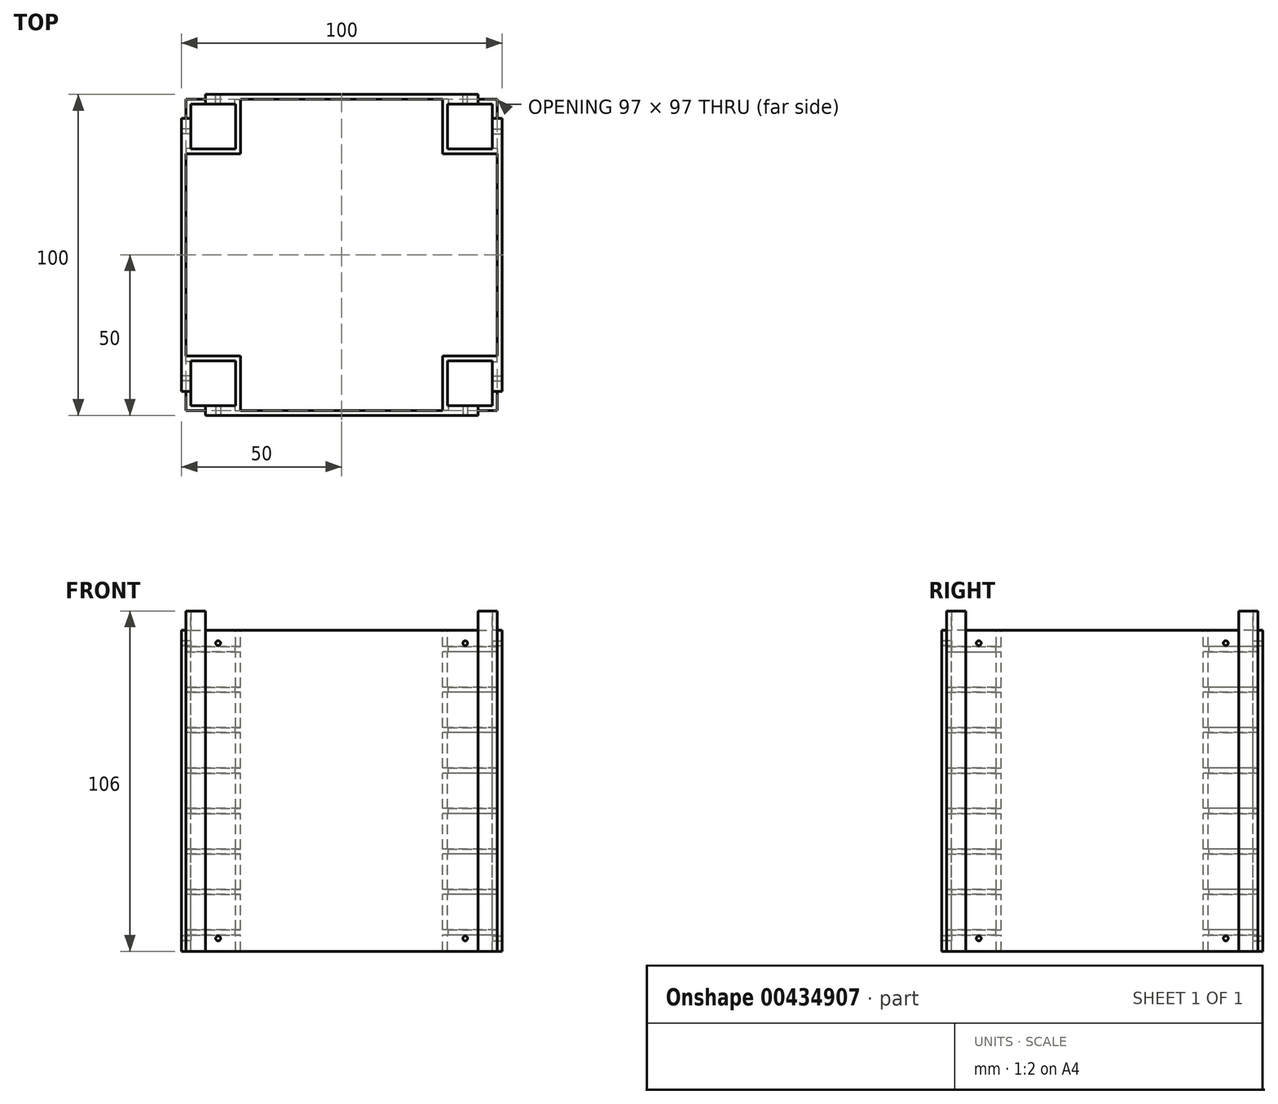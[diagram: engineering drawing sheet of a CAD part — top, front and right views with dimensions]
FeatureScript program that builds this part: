
annotation { "Feature Type Name" : "Feature", "Feature Type Description" : "" }
export const myFeature = defineFeature(function(context is Context, id is Id, definition is map)
    precondition{}
    {
        {
            var Q0;
            Q0=qCreatedBy(makeId("Top.planeOp"),FACE);
            var sketch = newSketch(context, id + "F0", { "sketchPlane" : qUnion([Q0])});
            skLineSegment(sketch, "E0", {"start": v(0, 97) * mm, "end": v(0, 80) * mm});
            skLineSegment(sketch, "E1", {"start": v(0, 80) * mm, "end": v(17, 80) * mm});
            skLineSegment(sketch, "E2", {"start": v(17, 80) * mm, "end": v(17, 97) * mm});
            skLineSegment(sketch, "E3", {"start": v(17, 97) * mm, "end": v(0, 97) * mm});
            skLineSegment(sketch, "E4", {"start": v(0, 97) * mm, "end": v(0, 95.5) * mm});
            skLineSegment(sketch, "E5", {"start": v(17, 97) * mm, "end": v(17, 95.5) * mm});
            skLineSegment(sketch, "E6", {"start": v(0, 80) * mm, "end": v(1.5, 80) * mm});
            skLineSegment(sketch, "E7", {"start": v(17, 80) * mm, "end": v(15.5, 80) * mm});
            skLineSegment(sketch, "E8", {"start": v(1.5, 95.5) * mm, "end": v(15.5, 95.5) * mm});
            skLineSegment(sketch, "E9", {"start": v(15.5, 81.5) * mm, "end": v(1.5, 81.5) * mm});
            skLineSegment(sketch, "E10", {"start": v(1.5, 95.5) * mm, "end": v(1.5, 81.5) * mm});
            skLineSegment(sketch, "E11", {"start": v(15.5, 95.5) * mm, "end": v(15.5, 81.5) * mm});
            skLineSegment(sketch, "E12.1.0.0", {"start": v(80, 97) * mm, "end": v(80, 95.5) * mm});
            skLineSegment(sketch, "E12.1.0.1", {"start": v(81.5, 95.5) * mm, "end": v(81.5, 81.5) * mm});
            skLineSegment(sketch, "E12.1.0.2", {"start": v(97, 80) * mm, "end": v(95.5, 80) * mm});
            skLineSegment(sketch, "E12.1.0.3", {"start": v(97, 97) * mm, "end": v(80, 97) * mm});
            skLineSegment(sketch, "E12.1.0.4", {"start": v(80, 97) * mm, "end": v(80, 80) * mm});
            skLineSegment(sketch, "E12.1.0.5", {"start": v(81.5, 95.5) * mm, "end": v(95.5, 95.5) * mm});
            skLineSegment(sketch, "E12.1.0.6", {"start": v(80, 80) * mm, "end": v(97, 80) * mm});
            skLineSegment(sketch, "E12.1.0.7", {"start": v(97, 80) * mm, "end": v(97, 97) * mm});
            skLineSegment(sketch, "E12.1.0.8", {"start": v(95.5, 81.5) * mm, "end": v(81.5, 81.5) * mm});
            skLineSegment(sketch, "E12.1.0.9", {"start": v(95.5, 95.5) * mm, "end": v(95.5, 81.5) * mm});
            skLineSegment(sketch, "E12.1.0.10", {"start": v(97, 97) * mm, "end": v(97, 95.5) * mm});
            skLineSegment(sketch, "E12.1.0.11", {"start": v(80, 80) * mm, "end": v(81.5, 80) * mm});
            skLineSegment(sketch, "E13.0.1.0", {"start": v(95.5, 15.5) * mm, "end": v(95.5, 1.5) * mm});
            skLineSegment(sketch, "E13.0.1.1", {"start": v(97, 0) * mm, "end": v(95.5, 0) * mm});
            skLineSegment(sketch, "E13.0.1.2", {"start": v(80, 0) * mm, "end": v(97, 0) * mm});
            skLineSegment(sketch, "E13.0.1.3", {"start": v(80, 17) * mm, "end": v(80, 15.5) * mm});
            skLineSegment(sketch, "E13.0.1.4", {"start": v(80, 17) * mm, "end": v(80, 0) * mm});
            skLineSegment(sketch, "E13.0.1.5", {"start": v(97, 0) * mm, "end": v(97, 17) * mm});
            skLineSegment(sketch, "E13.0.1.6", {"start": v(81.5, 15.5) * mm, "end": v(81.5, 1.5) * mm});
            skLineSegment(sketch, "E13.0.1.7", {"start": v(81.5, 15.5) * mm, "end": v(95.5, 15.5) * mm});
            skLineSegment(sketch, "E13.0.1.8", {"start": v(95.5, 1.5) * mm, "end": v(81.5, 1.5) * mm});
            skLineSegment(sketch, "E13.0.1.9", {"start": v(97, 17) * mm, "end": v(80, 17) * mm});
            skLineSegment(sketch, "E13.0.1.10", {"start": v(97, 17) * mm, "end": v(97, 15.5) * mm});
            skLineSegment(sketch, "E13.0.1.11", {"start": v(80, 0) * mm, "end": v(81.5, 0) * mm});
            skLineSegment(sketch, "E14.2.0.0", {"start": v(15.5, 1.5) * mm, "end": v(1.5, 1.5) * mm});
            skLineSegment(sketch, "E14.2.0.3", {"start": v(1.5, 15.5) * mm, "end": v(1.5, 1.5) * mm});
            skLineSegment(sketch, "E14.2.0.4", {"start": v(17, 17) * mm, "end": v(0, 17) * mm});
            skLineSegment(sketch, "E14.2.0.5", {"start": v(0, 0) * mm, "end": v(17, 0) * mm});
            skLineSegment(sketch, "E14.2.0.6", {"start": v(0, 17) * mm, "end": v(0, 0) * mm});
            skLineSegment(sketch, "E14.2.0.7", {"start": v(1.5, 15.5) * mm, "end": v(15.5, 15.5) * mm});
            skLineSegment(sketch, "E14.2.0.8", {"start": v(15.5, 15.5) * mm, "end": v(15.5, 1.5) * mm});
            skLineSegment(sketch, "E14.2.0.9", {"start": v(17, 0) * mm, "end": v(17, 17) * mm});
            skLineSegment(sketch, "E14.2.0.10", {"start": v(17, 0) * mm, "end": v(15.5, 0) * mm});
            skLineSegment(sketch, "E14.2.0.11", {"start": v(17, 17) * mm, "end": v(17, 15.5) * mm});
            skLineSegment(sketch, "E14.2.0.12", {"start": v(0, 17) * mm, "end": v(0, 15.5) * mm});
            skLineSegment(sketch, "E14.2.0.13", {"start": v(0, 0) * mm, "end": v(1.5, 0) * mm});
            skSolve(sketch);
        }
        {
            var Q0;
            Q0 = qSketchRegion(id + "F0", true);
            extrude(context, id + "F1", {"entities" : qUnion([Q0]), "oppositeDirection" : true, "depth" : 100 * mm});
        }
        {
            var Q0;
            Q0=makeQuery(id+"F1.opExtrude","CAP_FACE",FACE,{"disambiguationData":[OSD([sQuery(id+"F0.wireOp",EDGE,"E0"),sQuery(id+"F0.wireOp",EDGE,"E1"),sQuery(id+"F0.wireOp",EDGE,"E2"),sQuery(id+"F0.wireOp",EDGE,"E3"),sQuery(id+"F0.wireOp",EDGE,"E4"),sQuery(id+"F0.wireOp",EDGE,"E5"),sQuery(id+"F0.wireOp",EDGE,"E6"),sQuery(id+"F0.wireOp",EDGE,"E7"),sQuery(id+"F0.wireOp",EDGE,"E8"),sQuery(id+"F0.wireOp",EDGE,"E9"),sQuery(id+"F0.wireOp",EDGE,"E10"),sQuery(id+"F0.wireOp",EDGE,"E11")])],"isStart":true});
            var sketch = newSketch(context, id + "F2", { "sketchPlane" : qUnion([Q0])});
            skLineSegment(sketch, "E15", {"start": v(0, 97) * mm, "end": v(0, 91) * mm});
            skLineSegment(sketch, "E16", {"start": v(0, 91) * mm, "end": v(-1.5, 91) * mm});
            skLineSegment(sketch, "E17", {"start": v(0, 0) * mm, "end": v(0, 6) * mm});
            skLineSegment(sketch, "E18", {"start": v(0, 6) * mm, "end": v(-1.5, 6) * mm});
            skLineSegment(sketch, "E19", {"start": v(-1.5, 6) * mm, "end": v(-1.5, 91) * mm});
            skLineSegment(sketch, "E20", {"start": v(0, 91) * mm, "end": v(0, 6) * mm});
            skLineSegment(sketch, "E21", {"start": v(0, 0) * mm, "end": v(6, 0) * mm});
            skLineSegment(sketch, "E22", {"start": v(6, 0) * mm, "end": v(6, -1.5) * mm});
            skLineSegment(sketch, "E23", {"start": v(6, -1.5) * mm, "end": v(91, -1.5) * mm});
            skLineSegment(sketch, "E24", {"start": v(91, -1.5) * mm, "end": v(91, 0) * mm});
            skLineSegment(sketch, "E25", {"start": v(91, 0) * mm, "end": v(6, 0) * mm});
            skLineSegment(sketch, "E26.0", {"start": v(97, 97) * mm, "end": v(80, 97) * mm});
            skLineSegment(sketch, "E27.0", {"start": v(97, 80) * mm, "end": v(97, 97) * mm});
            skLineSegment(sketch, "E28.0", {"start": v(97, 17) * mm, "end": v(97, 0) * mm});
            skLineSegment(sketch, "E29.0", {"start": v(97, 17) * mm, "end": v(80, 17) * mm});
            skLineSegment(sketch, "E30", {"start": v(97, 97) * mm, "end": v(97, 91) * mm});
            skLineSegment(sketch, "E31", {"start": v(97, 91) * mm, "end": v(98.5, 91) * mm});
            skLineSegment(sketch, "E32", {"start": v(98.5, 91) * mm, "end": v(98.5, 6) * mm});
            skLineSegment(sketch, "E33", {"start": v(98.5, 6) * mm, "end": v(97, 6) * mm});
            skLineSegment(sketch, "E34", {"start": v(97, 6) * mm, "end": v(97, 80) * mm});
            skLineSegment(sketch, "E35", {"start": v(0, 97) * mm, "end": v(6, 97) * mm});
            skLineSegment(sketch, "E36", {"start": v(6, 97) * mm, "end": v(91, 97) * mm});
            skLineSegment(sketch, "E37", {"start": v(91, 97) * mm, "end": v(91, 98.5) * mm});
            skLineSegment(sketch, "E38", {"start": v(91, 98.5) * mm, "end": v(6, 98.5) * mm});
            skLineSegment(sketch, "E39", {"start": v(6, 98.5) * mm, "end": v(6, 97) * mm});
            skSolve(sketch);
        }
        {
            var Q0;
            Q0 = qSketchRegion(id + "F2", true);
            extrude(context, id + "F3", {"entities" : qUnion([Q0]), "oppositeDirection" : true, "depth" : 100 * mm, "offsetDistance" : 25 * mm});
        }
        {
            var Q0;
            Q0=makeQuery(id+"F1.opExtrude","CAP_FACE",FACE,{"disambiguationData":[OSD([sQuery(id+"F0.wireOp",EDGE,"E0"),sQuery(id+"F0.wireOp",EDGE,"E1"),sQuery(id+"F0.wireOp",EDGE,"E2"),sQuery(id+"F0.wireOp",EDGE,"E3"),sQuery(id+"F0.wireOp",EDGE,"E4"),sQuery(id+"F0.wireOp",EDGE,"E5"),sQuery(id+"F0.wireOp",EDGE,"E6"),sQuery(id+"F0.wireOp",EDGE,"E7"),sQuery(id+"F0.wireOp",EDGE,"E8"),sQuery(id+"F0.wireOp",EDGE,"E9"),sQuery(id+"F0.wireOp",EDGE,"E10"),sQuery(id+"F0.wireOp",EDGE,"E11")])],"isStart":true});
            var sketch = newSketch(context, id + "F4", { "sketchPlane" : qUnion([Q0])});
            skLineSegment(sketch, "E40.0", {"start": v(0, 97) * mm, "end": v(0, 91) * mm});
            skLineSegment(sketch, "E41.0", {"start": v(17, 97) * mm, "end": v(0, 97) * mm});
            skPoint(sketch, "E42.0", {"position": v(-0.75, 91) * mm});
            skLineSegment(sketch, "E43.0", {"start": v(0, 91) * mm, "end": v(-1.5, 91) * mm});
            skLineSegment(sketch, "E44.0", {"start": v(6, 98.5) * mm, "end": v(6, 97) * mm});
            skLineSegment(sketch, "E45.0.0", {"start": v(91, 98.5) * mm, "end": v(6, 98.5) * mm});
            skLineSegment(sketch, "E45.0.2", {"start": v(17, 97) * mm, "end": v(91, 97) * mm});
            skLineSegment(sketch, "E46.0", {"start": v(97, 97) * mm, "end": v(91, 97) * mm});
            skLineSegment(sketch, "E47.0", {"start": v(97, 91) * mm, "end": v(97, 97) * mm});
            skLineSegment(sketch, "E48.0", {"start": v(97, 6) * mm, "end": v(97, 0) * mm});
            skLineSegment(sketch, "E49.0", {"start": v(91, 0) * mm, "end": v(97, 0) * mm});
            skLineSegment(sketch, "E50.0", {"start": v(0, 6) * mm, "end": v(0, 0) * mm});
            skLineSegment(sketch, "E51.0", {"start": v(0, 0) * mm, "end": v(6, 0) * mm});
            skLineSegment(sketch, "E52.0", {"start": v(1.5, 6) * mm, "end": v(1.5, 1.5) * mm});
            skLineSegment(sketch, "E53.0", {"start": v(15.5, 1.5) * mm, "end": v(1.5, 1.5) * mm});
            skLineSegment(sketch, "E54.0", {"start": v(95.5, 6) * mm, "end": v(95.5, 1.5) * mm});
            skLineSegment(sketch, "E55.0", {"start": v(95.5, 95.5) * mm, "end": v(95.5, 91) * mm});
            skLineSegment(sketch, "E56.0", {"start": v(91, 95.5) * mm, "end": v(95.5, 95.5) * mm});
            skLineSegment(sketch, "E57.0", {"start": v(1.5, 95.5) * mm, "end": v(6, 95.5) * mm});
            skLineSegment(sketch, "E58.0", {"start": v(1.5, 95.5) * mm, "end": v(1.5, 81.5) * mm});
            skLineSegment(sketch, "E59", {"start": v(0, 91) * mm, "end": v(1.5, 91) * mm});
            skLineSegment(sketch, "E60", {"start": v(1.5, 91) * mm, "end": v(1.5, 95.5) * mm});
            skLineSegment(sketch, "E61", {"start": v(6, 95.5) * mm, "end": v(6, 97) * mm});
            skLineSegment(sketch, "E62", {"start": v(0, 97) * mm, "end": v(6, 97) * mm});
            skLineSegment(sketch, "E63", {"start": v(91, 97) * mm, "end": v(91, 95.5) * mm});
            skLineSegment(sketch, "E64", {"start": v(95.5, 91) * mm, "end": v(95.5, 95.5) * mm});
            skLineSegment(sketch, "E65", {"start": v(95.5, 91) * mm, "end": v(97, 91) * mm});
            skLineSegment(sketch, "E66", {"start": v(6, 0) * mm, "end": v(6, 1.5) * mm});
            skLineSegment(sketch, "E67", {"start": v(6, 1.5) * mm, "end": v(6, 0) * mm});
            skLineSegment(sketch, "E68", {"start": v(0, 6) * mm, "end": v(1.5, 6) * mm});
            skLineSegment(sketch, "E69", {"start": v(97, 6) * mm, "end": v(95.5, 6) * mm});
            skLineSegment(sketch, "E70", {"start": v(91, 0) * mm, "end": v(91, 1.5) * mm});
            skLineSegment(sketch, "E71", {"start": v(91, 1.5) * mm, "end": v(95.5, 1.5) * mm});
            skPoint(sketch, "E72.orphan", {"position": v(0, 80) * mm});
            skPoint(sketch, "E73.orphan", {"position": v(15.5, 95.5) * mm});
            skPoint(sketch, "E74.orphan", {"position": v(80, 97) * mm});
            skPoint(sketch, "E75.0.end.orphan", {"position": v(98.5, 91) * mm});
            skPoint(sketch, "E76.orphan", {"position": v(95.5, 81.5) * mm});
            skPoint(sketch, "E77.orphan", {"position": v(81.5, 95.5) * mm});
            skPoint(sketch, "E78.orphan", {"position": v(97, 80) * mm});
            skPoint(sketch, "E79.orphan", {"position": v(1.5, 15.5) * mm});
            skPoint(sketch, "E80.start.orphan", {"position": v(-1.5, 6) * mm});
            skPoint(sketch, "E81.orphan", {"position": v(0, 17) * mm});
            skPoint(sketch, "E82.0.end.orphan", {"position": v(6, -1.5) * mm});
            skPoint(sketch, "E83.orphan", {"position": v(17, 0) * mm});
            skPoint(sketch, "E84.orphan", {"position": v(80, 0) * mm});
            skPoint(sketch, "E85.0.start.orphan", {"position": v(91, -1.5) * mm});
            skPoint(sketch, "E86.0.start.orphan", {"position": v(98.5, 6) * mm});
            skPoint(sketch, "E87.orphan", {"position": v(97, 17) * mm});
            skPoint(sketch, "E88.orphan", {"position": v(95.5, 15.5) * mm});
            skPoint(sketch, "E89.orphan", {"position": v(81.5, 1.5) * mm});
            skSolve(sketch);
        }
        {
            var Q0;
            Q0 = qSketchRegion(id + "F4", true);
            extrude(context, id + "F5", {"entities" : qUnion([Q0]), "operationType" : NewBodyOperationType.ADD, "depth" : 6 * mm});
        }
        {
            var Q0;
            Q0=makeQuery(id+"F3.opExtrude","SWEPT_FACE",FACE,{"disambiguationData":[OSD([sQuery(id+"F2.wireOp",EDGE,"E32")])]});
            var sketch = newSketch(context, id + "F6", { "sketchPlane" : qUnion([Q0])});
            skCircle(sketch, "E90", {"center": v(10, -4) * mm, "radius": 0.75 * mm});
            skCircle(sketch, "E91", {"center": v(87, -4) * mm, "radius": 0.75 * mm});
            skCircle(sketch, "E92", {"center": v(87, -96) * mm, "radius": 0.75 * mm});
            skCircle(sketch, "E93", {"center": v(10, -96) * mm, "radius": 0.75 * mm});
            skSolve(sketch);
        }
        {
            var Q0;
            Q0 = qSketchRegion(id + "F6", true);
            extrude(context, id + "F7", {"entities" : qUnion([Q0]), "operationType" : NewBodyOperationType.REMOVE, "oppositeDirection" : true, "depth" : 10 * mm});
        }
        {
            var Q0;
            Q0=makeQuery(id+"F3.opExtrude","SWEPT_FACE",FACE,{"disambiguationData":[OSD([sQuery(id+"F2.wireOp",EDGE,"E38")])]});
            var sketch = newSketch(context, id + "F8", { "sketchPlane" : qUnion([Q0])});
            skPoint(sketch, "E94.0", {"position": v(-6, 0) * mm});
            skCircle(sketch, "E95", {"center": v(-87, -4) * mm, "radius": 0.75 * mm});
            skCircle(sketch, "E96", {"center": v(-10, -4) * mm, "radius": 0.75 * mm});
            skCircle(sketch, "E97", {"center": v(-10, -96) * mm, "radius": 0.75 * mm});
            skCircle(sketch, "E98", {"center": v(-87, -96) * mm, "radius": 0.75 * mm});
            skSolve(sketch);
        }
        {
            var Q0;
            Q0 = qSketchRegion(id + "F8", true);
            extrude(context, id + "F9", {"entities" : qUnion([Q0]), "operationType" : NewBodyOperationType.REMOVE, "oppositeDirection" : true, "depth" : 10 * mm});
        }
        {
            var Q0;
            Q0=makeQuery(id+"F3.opExtrude","SWEPT_FACE",FACE,{"disambiguationData":[OSD([sQuery(id+"F2.wireOp",EDGE,"E19")])]});
            var sketch = newSketch(context, id + "F10", { "sketchPlane" : qUnion([Q0])});
            skCircle(sketch, "E99", {"center": v(-87, -96) * mm, "radius": 0.75 * mm});
            skCircle(sketch, "E100", {"center": v(-10, -96) * mm, "radius": 0.75 * mm});
            skCircle(sketch, "E101", {"center": v(-10, -4) * mm, "radius": 0.75 * mm});
            skCircle(sketch, "E102", {"center": v(-87, -4) * mm, "radius": 0.75 * mm});
            skSolve(sketch);
        }
        {
            var Q0;
            Q0 = qSketchRegion(id + "F10", true);
            extrude(context, id + "F11", {"entities" : qUnion([Q0]), "operationType" : NewBodyOperationType.REMOVE, "oppositeDirection" : true, "depth" : 10 * mm});
        }
        {
            var Q0;
            Q0=makeQuery(id+"F3.opExtrude","SWEPT_FACE",FACE,{"disambiguationData":[OSD([sQuery(id+"F2.wireOp",EDGE,"E23")])]});
            var sketch = newSketch(context, id + "F12", { "sketchPlane" : qUnion([Q0])});
            skCircle(sketch, "E103", {"center": v(10, -4) * mm, "radius": 0.75 * mm});
            skCircle(sketch, "E104", {"center": v(87, -4) * mm, "radius": 0.75 * mm});
            skCircle(sketch, "E105", {"center": v(87, -96) * mm, "radius": 0.75 * mm});
            skCircle(sketch, "E106", {"center": v(10, -96) * mm, "radius": 0.75 * mm});
            skSolve(sketch);
        }
        {
            var Q0;
            Q0 = qSketchRegion(id + "F12", true);
            extrude(context, id + "F13", {"entities" : qUnion([Q0]), "operationType" : NewBodyOperationType.REMOVE, "oppositeDirection" : true, "depth" : 10 * mm});
        }
        {
            var Q0;
            Q0=makeQuery(id+"F1.opExtrude","SWEPT_FACE",FACE,{"disambiguationData":[OSD([sQuery(id+"F0.wireOp",EDGE,"E1"),sQuery(id+"F0.wireOp",EDGE,"E6"),sQuery(id+"F0.wireOp",EDGE,"E7")])]});
            var sketch = newSketch(context, id + "F14", { "sketchPlane" : qUnion([Q0])});
            skLineSegment(sketch, "E107", {"start": v(0, 0) * mm, "end": v(0, -5.11) * mm});
            skLineSegment(sketch, "E108", {"start": v(0, -5.11) * mm, "end": v(17, -5.11) * mm});
            skLineSegment(sketch, "E109", {"start": v(17, -5.11) * mm, "end": v(17, -6.7) * mm});
            skLineSegment(sketch, "E110", {"start": v(17, -6.7) * mm, "end": v(0, -6.7) * mm});
            skLineSegment(sketch, "E111", {"start": v(0, -6.7) * mm, "end": v(0, -5.11) * mm});
            skSolve(sketch);
        }
        {
            var Q0;
            Q0 = qSketchRegion(id + "F14", true);
            extrude(context, id + "F15", {"entities" : qUnion([Q0]), "operationType" : NewBodyOperationType.REMOVE, "oppositeDirection" : true, "depth" : 1.8 * mm});
        }
        {
            var Q0;
            Q0=makeQuery(id+"F1.opExtrude","SWEPT_FACE",FACE,{"disambiguationData":[OSD([sQuery(id+"F0.wireOp",EDGE,"E2"),sQuery(id+"F0.wireOp",EDGE,"E5")])]});
            var sketch = newSketch(context, id + "F16", { "sketchPlane" : qUnion([Q0])});
            skLineSegment(sketch, "E112", {"start": v(80, -5.11) * mm, "end": v(97, -5.11) * mm});
            skLineSegment(sketch, "E113", {"start": v(97, -5.11) * mm, "end": v(97, -6.7) * mm});
            skLineSegment(sketch, "E114", {"start": v(97, -6.7) * mm, "end": v(80, -6.7) * mm});
            skLineSegment(sketch, "E115", {"start": v(80, -6.7) * mm, "end": v(80, -5.11) * mm});
            skSolve(sketch);
        }
        {
            var Q0;
            Q0 = qSketchRegion(id + "F16", true);
            extrude(context, id + "F17", {"entities" : qUnion([Q0]), "operationType" : NewBodyOperationType.REMOVE, "oppositeDirection" : true, "depth" : 1.8 * mm});
        }
        {
            var Q0;
            {var subQ4=sQuery(id+"F0.wireOp",EDGE,"E7");var subQ5=sQuery(id+"F0.wireOp",EDGE,"E6");var subQ6=sQuery(id+"F0.wireOp",EDGE,"E1");Q0=makeQuery(id+"F15.boolean.opBoolean","SPLIT",FACE,{"disambiguationData":[TD([makeQuery(id+"F15.opExtrude","SWEPT_FACE",FACE,{"disambiguationData":[OSD([sQuery(id+"F14.wireOp",EDGE,"E110")])]})])],"derivedFrom":makeQuery(id+"F1.opExtrude","SWEPT_FACE",FACE,{"disambiguationData":[OSD([subQ6,subQ5,subQ4])]})});}
            var sketch = newSketch(context, id + "F18", { "sketchPlane" : qUnion([Q0])});
            skLineSegment(sketch, "E116", {"start": v(0, -17.7) * mm, "end": v(17, -17.7) * mm});
            skLineSegment(sketch, "E117", {"start": v(0, -17.7) * mm, "end": v(0, -19.3) * mm});
            skLineSegment(sketch, "E118", {"start": v(0, -19.3) * mm, "end": v(17, -19.3) * mm});
            skLineSegment(sketch, "E119", {"start": v(17, -19.3) * mm, "end": v(17, -17.7) * mm});
            skLineSegment(sketch, "E120", {"start": v(0, -19.3) * mm, "end": v(0, -30.3) * mm});
            skLineSegment(sketch, "E121", {"start": v(0, -30.3) * mm, "end": v(17, -30.3) * mm});
            skLineSegment(sketch, "E122", {"start": v(17, -30.3) * mm, "end": v(17, -31.91) * mm});
            skLineSegment(sketch, "E123", {"start": v(17, -31.91) * mm, "end": v(0, -31.91) * mm});
            skLineSegment(sketch, "E124", {"start": v(0, -31.91) * mm, "end": v(0, -30.3) * mm});
            skLineSegment(sketch, "E125", {"start": v(0, -31.91) * mm, "end": v(0, -42.91) * mm});
            skLineSegment(sketch, "E126", {"start": v(0, -42.91) * mm, "end": v(17, -42.91) * mm});
            skLineSegment(sketch, "E127", {"start": v(17, -42.91) * mm, "end": v(17, -44.5) * mm});
            skLineSegment(sketch, "E128", {"start": v(17, -44.5) * mm, "end": v(0, -44.5) * mm});
            skLineSegment(sketch, "E129", {"start": v(0, -44.5) * mm, "end": v(0, -42.91) * mm});
            skLineSegment(sketch, "E130", {"start": v(0, -44.5) * mm, "end": v(0, -55.51) * mm});
            skLineSegment(sketch, "E131", {"start": v(0, -55.51) * mm, "end": v(17, -55.51) * mm});
            skLineSegment(sketch, "E132", {"start": v(17, -55.51) * mm, "end": v(17, -57.11) * mm});
            skLineSegment(sketch, "E133", {"start": v(17, -57.11) * mm, "end": v(0, -57.11) * mm});
            skLineSegment(sketch, "E134", {"start": v(0, -57.11) * mm, "end": v(0, -55.51) * mm});
            skLineSegment(sketch, "E135", {"start": v(0, -57.11) * mm, "end": v(0, -68.11) * mm});
            skLineSegment(sketch, "E136", {"start": v(0, -68.11) * mm, "end": v(17, -68.11) * mm});
            skLineSegment(sketch, "E137", {"start": v(17, -68.11) * mm, "end": v(17, -69.71) * mm});
            skLineSegment(sketch, "E138", {"start": v(17, -69.71) * mm, "end": v(0, -69.71) * mm});
            skLineSegment(sketch, "E139", {"start": v(0, -69.71) * mm, "end": v(0, -68.11) * mm});
            skLineSegment(sketch, "E140", {"start": v(0, -69.71) * mm, "end": v(0, -80.71) * mm});
            skLineSegment(sketch, "E141", {"start": v(0, -80.71) * mm, "end": v(17, -80.71) * mm});
            skLineSegment(sketch, "E142", {"start": v(17, -80.71) * mm, "end": v(17, -82.31) * mm});
            skLineSegment(sketch, "E143", {"start": v(17, -82.31) * mm, "end": v(0, -82.31) * mm});
            skLineSegment(sketch, "E144", {"start": v(0, -82.31) * mm, "end": v(0, -80.71) * mm});
            skLineSegment(sketch, "E145", {"start": v(0, -82.31) * mm, "end": v(0, -93.31) * mm});
            skLineSegment(sketch, "E146", {"start": v(0, -93.31) * mm, "end": v(17, -93.31) * mm});
            skLineSegment(sketch, "E147", {"start": v(17, -93.31) * mm, "end": v(17, -94.91) * mm});
            skLineSegment(sketch, "E148", {"start": v(17, -94.91) * mm, "end": v(0, -94.91) * mm});
            skLineSegment(sketch, "E149", {"start": v(0, -94.91) * mm, "end": v(0, -93.31) * mm});
            skSolve(sketch);
        }
        {
            var Q0;
            Q0 = qSketchRegion(id + "F18", true);
            extrude(context, id + "F19", {"entities" : qUnion([Q0]), "operationType" : NewBodyOperationType.REMOVE, "oppositeDirection" : true, "depth" : 1.8 * mm});
        }
        {
            var Q0;
            {var subQ4=sQuery(id+"F0.wireOp",EDGE,"E5");var subQ5=sQuery(id+"F0.wireOp",EDGE,"E2");Q0=makeQuery(id+"F17.boolean.opBoolean","SPLIT",FACE,{"disambiguationData":[TD([makeQuery(id+"F15.boolean.opBoolean","COPY",FACE,{"derivedFrom":makeQuery(id+"F15.opExtrude","SWEPT_FACE",FACE,{"disambiguationData":[OSD([sQuery(id+"F14.wireOp",EDGE,"E110")])]})})])],"derivedFrom":makeQuery(id+"F1.opExtrude","SWEPT_FACE",FACE,{"disambiguationData":[OSD([subQ5,subQ4])]})});}
            var sketch = newSketch(context, id + "F20", { "sketchPlane" : qUnion([Q0])});
            skLineSegment(sketch, "E150", {"start": v(80, -17.7) * mm, "end": v(97, -17.7) * mm});
            skLineSegment(sketch, "E151", {"start": v(97, -17.7) * mm, "end": v(97, -19.3) * mm});
            skLineSegment(sketch, "E152", {"start": v(97, -19.3) * mm, "end": v(80, -19.3) * mm});
            skLineSegment(sketch, "E153", {"start": v(80, -19.3) * mm, "end": v(80, -17.7) * mm});
            skLineSegment(sketch, "E154", {"start": v(80, -30.31) * mm, "end": v(97, -30.31) * mm});
            skLineSegment(sketch, "E155", {"start": v(97, -30.31) * mm, "end": v(97, -31.9) * mm});
            skLineSegment(sketch, "E156", {"start": v(97, -31.9) * mm, "end": v(80, -31.9) * mm});
            skLineSegment(sketch, "E157", {"start": v(80, -31.9) * mm, "end": v(80, -30.31) * mm});
            skLineSegment(sketch, "E158", {"start": v(80, -42.91) * mm, "end": v(97, -42.91) * mm});
            skLineSegment(sketch, "E159", {"start": v(97, -42.91) * mm, "end": v(97, -44.5) * mm});
            skLineSegment(sketch, "E160", {"start": v(97, -44.5) * mm, "end": v(80, -44.5) * mm});
            skLineSegment(sketch, "E161", {"start": v(80, -44.5) * mm, "end": v(80, -42.91) * mm});
            skLineSegment(sketch, "E162", {"start": v(81.8, -55.51) * mm, "end": v(97, -55.51) * mm});
            skLineSegment(sketch, "E163", {"start": v(97, -55.51) * mm, "end": v(80, -55.51) * mm});
            skLineSegment(sketch, "E164", {"start": v(80, -55.51) * mm, "end": v(80, -57.11) * mm});
            skLineSegment(sketch, "E165", {"start": v(80, -57.11) * mm, "end": v(97, -57.11) * mm});
            skLineSegment(sketch, "E166", {"start": v(97, -57.11) * mm, "end": v(97, -55.51) * mm});
            skLineSegment(sketch, "E167", {"start": v(80, -68.11) * mm, "end": v(97, -68.11) * mm});
            skLineSegment(sketch, "E168", {"start": v(97, -68.11) * mm, "end": v(97, -69.71) * mm});
            skLineSegment(sketch, "E169", {"start": v(97, -69.71) * mm, "end": v(80, -69.71) * mm});
            skLineSegment(sketch, "E170", {"start": v(80, -69.71) * mm, "end": v(80, -68.11) * mm});
            skLineSegment(sketch, "E171", {"start": v(80, -80.71) * mm, "end": v(97, -80.71) * mm});
            skLineSegment(sketch, "E172", {"start": v(97, -80.71) * mm, "end": v(97, -82.31) * mm});
            skLineSegment(sketch, "E173", {"start": v(97, -82.31) * mm, "end": v(80, -82.31) * mm});
            skLineSegment(sketch, "E174", {"start": v(80, -82.31) * mm, "end": v(80, -80.71) * mm});
            skLineSegment(sketch, "E175", {"start": v(80, -93.31) * mm, "end": v(97, -93.31) * mm});
            skLineSegment(sketch, "E176", {"start": v(97, -93.31) * mm, "end": v(97, -94.91) * mm});
            skLineSegment(sketch, "E177", {"start": v(97, -94.91) * mm, "end": v(80, -94.91) * mm});
            skLineSegment(sketch, "E178", {"start": v(80, -94.91) * mm, "end": v(80, -93.31) * mm});
            skSolve(sketch);
        }
        {
            var Q0;
            Q0 = qSketchRegion(id + "F20", true);
            extrude(context, id + "F21", {"entities" : qUnion([Q0]), "operationType" : NewBodyOperationType.REMOVE, "oppositeDirection" : true, "depth" : 1.8 * mm});
        }
        {
            var Q0;
            Q0=makeQuery(id+"F1.opExtrude","SWEPT_FACE",FACE,{"disambiguationData":[OSD([sQuery(id+"F0.wireOp",EDGE,"E12.1.0.6"),sQuery(id+"F0.wireOp",EDGE,"E12.1.0.11")])]});
            var sketch = newSketch(context, id + "F22", { "sketchPlane" : qUnion([Q0])});
            skPoint(sketch, "E179.0", {"position": v(17, -5.11) * mm});
            skPoint(sketch, "E180.0", {"position": v(17, -6.7) * mm});
            skPoint(sketch, "E181.0", {"position": v(17, -17.7) * mm});
            skPoint(sketch, "E182.0", {"position": v(17, -19.3) * mm});
            skPoint(sketch, "E183.0", {"position": v(17, -30.31) * mm});
            skPoint(sketch, "E184.0", {"position": v(17, -31.9) * mm});
            skPoint(sketch, "E185.0", {"position": v(17, -42.91) * mm});
            skPoint(sketch, "E186.0", {"position": v(17, -44.5) * mm});
            skPoint(sketch, "E187.0", {"position": v(17, -55.51) * mm});
            skPoint(sketch, "E188.0", {"position": v(17, -57.11) * mm});
            skPoint(sketch, "E189.0", {"position": v(17, -68.11) * mm});
            skPoint(sketch, "E190.0", {"position": v(17, -69.71) * mm});
            skPoint(sketch, "E191.0", {"position": v(17, -82.31) * mm});
            skPoint(sketch, "E192.0", {"position": v(17, -80.71) * mm});
            skPoint(sketch, "E193.0", {"position": v(17, -93.31) * mm});
            skPoint(sketch, "E194.0", {"position": v(17, -94.91) * mm});
            skPoint(sketch, "E195.0", {"position": v(17, -100) * mm});
            skLineSegment(sketch, "E196", {"start": v(80, -5.11) * mm, "end": v(97, -5.11) * mm});
            skLineSegment(sketch, "E197", {"start": v(97, -5.11) * mm, "end": v(97, -6.7) * mm});
            skLineSegment(sketch, "E198", {"start": v(97, -6.7) * mm, "end": v(80, -6.7) * mm});
            skLineSegment(sketch, "E199", {"start": v(80, -6.7) * mm, "end": v(80, -5.11) * mm});
            skLineSegment(sketch, "E200", {"start": v(80, -17.7) * mm, "end": v(97, -17.7) * mm});
            skLineSegment(sketch, "E201", {"start": v(97, -17.7) * mm, "end": v(97, -19.3) * mm});
            skLineSegment(sketch, "E202", {"start": v(97, -19.3) * mm, "end": v(80, -19.3) * mm});
            skLineSegment(sketch, "E203", {"start": v(80, -19.3) * mm, "end": v(80, -17.7) * mm});
            skLineSegment(sketch, "E204", {"start": v(80, -30.31) * mm, "end": v(97, -30.31) * mm});
            skLineSegment(sketch, "E205", {"start": v(80, -30.31) * mm, "end": v(80, -31.9) * mm});
            skLineSegment(sketch, "E206", {"start": v(97, -30.31) * mm, "end": v(97, -31.9) * mm});
            skLineSegment(sketch, "E207", {"start": v(97, -31.9) * mm, "end": v(80, -31.9) * mm});
            skLineSegment(sketch, "E208", {"start": v(80, -42.91) * mm, "end": v(97, -42.91) * mm});
            skLineSegment(sketch, "E209", {"start": v(97, -42.91) * mm, "end": v(97, -44.5) * mm});
            skLineSegment(sketch, "E210", {"start": v(97, -44.5) * mm, "end": v(80, -44.5) * mm});
            skLineSegment(sketch, "E211", {"start": v(80, -42.91) * mm, "end": v(80, -44.5) * mm});
            skLineSegment(sketch, "E212", {"start": v(80, -55.51) * mm, "end": v(97, -55.51) * mm});
            skPoint(sketch, "E212.endSnap0", {"position": v(97, -50) * mm});
            skLineSegment(sketch, "E213", {"start": v(97, -55.51) * mm, "end": v(97, -57.11) * mm});
            skLineSegment(sketch, "E214", {"start": v(97, -57.11) * mm, "end": v(80, -57.11) * mm});
            skLineSegment(sketch, "E215", {"start": v(80, -57.11) * mm, "end": v(80, -55.51) * mm});
            skLineSegment(sketch, "E216", {"start": v(80, -68.11) * mm, "end": v(97, -68.11) * mm});
            skLineSegment(sketch, "E217", {"start": v(80, -80.71) * mm, "end": v(97, -80.71) * mm});
            skLineSegment(sketch, "E218", {"start": v(97, -80.71) * mm, "end": v(97, -82.31) * mm});
            skLineSegment(sketch, "E219", {"start": v(97, -82.31) * mm, "end": v(80, -82.31) * mm});
            skLineSegment(sketch, "E220", {"start": v(80, -82.31) * mm, "end": v(80, -80.71) * mm});
            skLineSegment(sketch, "E221", {"start": v(80, -93.31) * mm, "end": v(97, -93.31) * mm});
            skLineSegment(sketch, "E222", {"start": v(97, -93.31) * mm, "end": v(97, -94.91) * mm});
            skLineSegment(sketch, "E223", {"start": v(97, -94.91) * mm, "end": v(80, -94.91) * mm});
            skLineSegment(sketch, "E224", {"start": v(80, -94.91) * mm, "end": v(80, -93.31) * mm});
            skLineSegment(sketch, "E225", {"start": v(97, -68.11) * mm, "end": v(97, -69.71) * mm});
            skLineSegment(sketch, "E226", {"start": v(97, -69.71) * mm, "end": v(80, -69.71) * mm});
            skLineSegment(sketch, "E227", {"start": v(80, -69.71) * mm, "end": v(80, -68.11) * mm});
            skSolve(sketch);
        }
        {
            var Q0;
            Q0 = qSketchRegion(id + "F22", true);
            extrude(context, id + "F23", {"entities" : qUnion([Q0]), "operationType" : NewBodyOperationType.REMOVE, "oppositeDirection" : true, "depth" : 1.8 * mm});
        }
        {
            var Q0;
            Q0=makeQuery(id+"F1.opExtrude","SWEPT_FACE",FACE,{"disambiguationData":[OSD([sQuery(id+"F0.wireOp",EDGE,"E12.1.0.4")])]});
            var sketch = newSketch(context, id + "F24", { "sketchPlane" : qUnion([Q0])});
            skLineSegment(sketch, "E228", {"start": v(-97, -5.11) * mm, "end": v(-80, -5.11) * mm});
            skLineSegment(sketch, "E229", {"start": v(-97, -5.11) * mm, "end": v(-97, -6.7) * mm});
            skLineSegment(sketch, "E230", {"start": v(-80, -6.7) * mm, "end": v(-97, -6.7) * mm});
            skLineSegment(sketch, "E231", {"start": v(-80, -6.7) * mm, "end": v(-80, -5.11) * mm});
            skLineSegment(sketch, "E232", {"start": v(-97, -17.7) * mm, "end": v(-80, -17.7) * mm});
            skLineSegment(sketch, "E233", {"start": v(-97, -17.7) * mm, "end": v(-97, -19.3) * mm});
            skLineSegment(sketch, "E234", {"start": v(-80, -19.3) * mm, "end": v(-97, -19.3) * mm});
            skLineSegment(sketch, "E235", {"start": v(-80, -19.3) * mm, "end": v(-80, -17.7) * mm});
            skLineSegment(sketch, "E236", {"start": v(-97, -30.31) * mm, "end": v(-80, -30.3) * mm});
            skLineSegment(sketch, "E237", {"start": v(-97, -30.31) * mm, "end": v(-97, -31.9) * mm});
            skLineSegment(sketch, "E238", {"start": v(-80, -31.9) * mm, "end": v(-97, -31.9) * mm});
            skLineSegment(sketch, "E239", {"start": v(-80, -31.9) * mm, "end": v(-80, -30.31) * mm});
            skLineSegment(sketch, "E240", {"start": v(-97, -42.91) * mm, "end": v(-80, -42.91) * mm});
            skLineSegment(sketch, "E241", {"start": v(-97, -42.91) * mm, "end": v(-97, -44.5) * mm});
            skLineSegment(sketch, "E242", {"start": v(-80, -44.5) * mm, "end": v(-97, -44.5) * mm});
            skLineSegment(sketch, "E243", {"start": v(-80, -44.5) * mm, "end": v(-80, -42.91) * mm});
            skLineSegment(sketch, "E244", {"start": v(-97, -55.51) * mm, "end": v(-80, -55.51) * mm});
            skLineSegment(sketch, "E245", {"start": v(-97, -55.51) * mm, "end": v(-97, -57.11) * mm});
            skLineSegment(sketch, "E246", {"start": v(-80, -57.11) * mm, "end": v(-97, -57.11) * mm});
            skLineSegment(sketch, "E247", {"start": v(-80, -57.11) * mm, "end": v(-80, -55.51) * mm});
            skLineSegment(sketch, "E248", {"start": v(-97, -68.11) * mm, "end": v(-80, -68.11) * mm});
            skLineSegment(sketch, "E249", {"start": v(-97, -68.11) * mm, "end": v(-97, -69.71) * mm});
            skLineSegment(sketch, "E250", {"start": v(-80, -69.71) * mm, "end": v(-97, -69.71) * mm});
            skLineSegment(sketch, "E251", {"start": v(-80, -69.71) * mm, "end": v(-80, -68.11) * mm});
            skLineSegment(sketch, "E252", {"start": v(-97, -80.71) * mm, "end": v(-80, -80.71) * mm});
            skLineSegment(sketch, "E253", {"start": v(-97, -80.71) * mm, "end": v(-97, -82.31) * mm});
            skLineSegment(sketch, "E254", {"start": v(-80, -82.31) * mm, "end": v(-97, -82.31) * mm});
            skLineSegment(sketch, "E255", {"start": v(-80, -82.31) * mm, "end": v(-80, -80.71) * mm});
            skLineSegment(sketch, "E256", {"start": v(-97, -93.31) * mm, "end": v(-80, -93.31) * mm});
            skLineSegment(sketch, "E257", {"start": v(-97, -93.31) * mm, "end": v(-97, -94.91) * mm});
            skLineSegment(sketch, "E258", {"start": v(-80, -94.91) * mm, "end": v(-97, -94.91) * mm});
            skLineSegment(sketch, "E259", {"start": v(-80, -94.91) * mm, "end": v(-80, -93.31) * mm});
            skSolve(sketch);
        }
        {
            var Q0;
            Q0 = qSketchRegion(id + "F24", true);
            extrude(context, id + "F25", {"entities" : qUnion([Q0]), "operationType" : NewBodyOperationType.REMOVE, "oppositeDirection" : true, "depth" : 1.8 * mm, "offsetDistance" : 25 * mm});
        }
        {
            var Q0;
            Q0=makeQuery(id+"F1.opExtrude","SWEPT_FACE",FACE,{"disambiguationData":[OSD([sQuery(id+"F0.wireOp",EDGE,"E13.0.1.4")])]});
            var sketch = newSketch(context, id + "F26", { "sketchPlane" : qUnion([Q0])});
            skPoint(sketch, "E260.0", {"position": v(-80, -5.11) * mm});
            skPoint(sketch, "E261.0", {"position": v(-80, -6.7) * mm});
            skPoint(sketch, "E262.0", {"position": v(-80, -17.7) * mm});
            skPoint(sketch, "E263.0", {"position": v(-80, -19.3) * mm});
            skPoint(sketch, "E264.0", {"position": v(-80, -30.31) * mm});
            skPoint(sketch, "E265.0", {"position": v(-80, -31.9) * mm});
            skPoint(sketch, "E266.0", {"position": v(-80, -42.91) * mm});
            skPoint(sketch, "E267.0", {"position": v(-80, -44.5) * mm});
            skPoint(sketch, "E268.0", {"position": v(-80, -55.51) * mm});
            skPoint(sketch, "E269.0", {"position": v(-80, -57.11) * mm});
            skPoint(sketch, "E270.0", {"position": v(-80, -68.11) * mm});
            skPoint(sketch, "E271.0", {"position": v(-80, -69.71) * mm});
            skPoint(sketch, "E272.0", {"position": v(-80, -80.71) * mm});
            skPoint(sketch, "E273.0", {"position": v(-80, -82.31) * mm});
            skPoint(sketch, "E274.0", {"position": v(-80, -93.31) * mm});
            skPoint(sketch, "E275.0", {"position": v(-80, -94.91) * mm});
            skLineSegment(sketch, "E276", {"start": v(-17, -5.11) * mm, "end": v(0, -5.11) * mm});
            skLineSegment(sketch, "E277", {"start": v(0, -5.11) * mm, "end": v(0, -6.7) * mm});
            skLineSegment(sketch, "E278", {"start": v(0, -6.7) * mm, "end": v(-17, -6.7) * mm});
            skLineSegment(sketch, "E279", {"start": v(-17, -6.7) * mm, "end": v(-17, -5.11) * mm});
            skLineSegment(sketch, "E280", {"start": v(-17, -17.7) * mm, "end": v(0, -17.7) * mm});
            skLineSegment(sketch, "E281", {"start": v(0, -17.7) * mm, "end": v(0, -19.3) * mm});
            skLineSegment(sketch, "E282", {"start": v(0, -19.3) * mm, "end": v(-17, -19.3) * mm});
            skLineSegment(sketch, "E283", {"start": v(-17, -19.3) * mm, "end": v(-17, -17.7) * mm});
            skLineSegment(sketch, "E284", {"start": v(-17, -30.31) * mm, "end": v(0, -30.31) * mm});
            skLineSegment(sketch, "E285", {"start": v(0, -30.31) * mm, "end": v(0, -31.9) * mm});
            skLineSegment(sketch, "E286", {"start": v(0, -31.9) * mm, "end": v(-17, -31.9) * mm});
            skLineSegment(sketch, "E287", {"start": v(-17, -31.9) * mm, "end": v(-17, -30.31) * mm});
            skLineSegment(sketch, "E288", {"start": v(-17, -42.91) * mm, "end": v(0, -42.91) * mm});
            skLineSegment(sketch, "E289", {"start": v(0, -42.91) * mm, "end": v(0, -44.5) * mm});
            skLineSegment(sketch, "E290", {"start": v(0, -44.5) * mm, "end": v(-17, -44.5) * mm});
            skLineSegment(sketch, "E291", {"start": v(-17, -44.5) * mm, "end": v(-17, -42.91) * mm});
            skLineSegment(sketch, "E292", {"start": v(-17, -55.51) * mm, "end": v(0, -55.51) * mm});
            skLineSegment(sketch, "E293", {"start": v(0, -55.51) * mm, "end": v(0, -57.11) * mm});
            skLineSegment(sketch, "E294", {"start": v(0, -57.11) * mm, "end": v(-17, -57.11) * mm});
            skLineSegment(sketch, "E295", {"start": v(-17, -57.11) * mm, "end": v(-17, -55.51) * mm});
            skLineSegment(sketch, "E296", {"start": v(-17, -68.11) * mm, "end": v(0, -68.11) * mm});
            skLineSegment(sketch, "E297", {"start": v(0, -68.11) * mm, "end": v(0, -69.71) * mm});
            skLineSegment(sketch, "E298", {"start": v(0, -69.71) * mm, "end": v(-17, -69.71) * mm});
            skLineSegment(sketch, "E299", {"start": v(-17, -69.71) * mm, "end": v(-17, -68.11) * mm});
            skLineSegment(sketch, "E300", {"start": v(-17, -80.71) * mm, "end": v(0, -80.71) * mm});
            skLineSegment(sketch, "E301", {"start": v(0, -80.71) * mm, "end": v(0, -82.31) * mm});
            skLineSegment(sketch, "E302", {"start": v(0, -82.31) * mm, "end": v(-17, -82.31) * mm});
            skLineSegment(sketch, "E303", {"start": v(-17, -82.31) * mm, "end": v(-17, -80.71) * mm});
            skLineSegment(sketch, "E304", {"start": v(-17, -93.31) * mm, "end": v(0, -93.31) * mm});
            skLineSegment(sketch, "E305", {"start": v(0, -93.31) * mm, "end": v(0, -94.91) * mm});
            skLineSegment(sketch, "E306", {"start": v(0, -94.91) * mm, "end": v(-17, -94.91) * mm});
            skLineSegment(sketch, "E307", {"start": v(-17, -94.91) * mm, "end": v(-17, -93.31) * mm});
            skSolve(sketch);
        }
        {
            var Q0;
            Q0 = qSketchRegion(id + "F26", true);
            extrude(context, id + "F27", {"entities" : qUnion([Q0]), "operationType" : NewBodyOperationType.REMOVE, "oppositeDirection" : true, "depth" : 1.8 * mm});
        }
        {
            var Q0;
            Q0=makeQuery(id+"F1.opExtrude","SWEPT_FACE",FACE,{"disambiguationData":[OSD([sQuery(id+"F0.wireOp",EDGE,"E13.0.1.9")])]});
            var sketch = newSketch(context, id + "F28", { "sketchPlane" : qUnion([Q0])});
            skLineSegment(sketch, "E308", {"start": v(-80, -5.11) * mm, "end": v(-97, -5.11) * mm});
            skLineSegment(sketch, "E309", {"start": v(-97, -5.11) * mm, "end": v(-97, -6.7) * mm});
            skLineSegment(sketch, "E310", {"start": v(-97, -6.7) * mm, "end": v(-80, -6.7) * mm});
            skLineSegment(sketch, "E311", {"start": v(-80, -6.7) * mm, "end": v(-80, -5.11) * mm});
            skLineSegment(sketch, "E312", {"start": v(-80, -17.7) * mm, "end": v(-97, -17.7) * mm});
            skLineSegment(sketch, "E313", {"start": v(-97, -17.7) * mm, "end": v(-97, -19.3) * mm});
            skLineSegment(sketch, "E314", {"start": v(-97, -19.3) * mm, "end": v(-80, -19.3) * mm});
            skLineSegment(sketch, "E315", {"start": v(-80, -19.3) * mm, "end": v(-80, -17.7) * mm});
            skLineSegment(sketch, "E316", {"start": v(-80, -30.31) * mm, "end": v(-97, -30.31) * mm});
            skLineSegment(sketch, "E317", {"start": v(-97, -30.31) * mm, "end": v(-97, -31.9) * mm});
            skLineSegment(sketch, "E318", {"start": v(-97, -31.9) * mm, "end": v(-80, -31.9) * mm});
            skLineSegment(sketch, "E319", {"start": v(-80, -31.9) * mm, "end": v(-80, -30.31) * mm});
            skLineSegment(sketch, "E320", {"start": v(-80, -42.91) * mm, "end": v(-97, -42.91) * mm});
            skLineSegment(sketch, "E321", {"start": v(-97, -42.91) * mm, "end": v(-97, -44.5) * mm});
            skLineSegment(sketch, "E322", {"start": v(-97, -44.5) * mm, "end": v(-80, -44.5) * mm});
            skLineSegment(sketch, "E323", {"start": v(-80, -44.5) * mm, "end": v(-80, -42.91) * mm});
            skLineSegment(sketch, "E324", {"start": v(-80, -55.51) * mm, "end": v(-97, -55.51) * mm});
            skLineSegment(sketch, "E325", {"start": v(-97, -55.51) * mm, "end": v(-97, -57.11) * mm});
            skLineSegment(sketch, "E326", {"start": v(-97, -57.11) * mm, "end": v(-80, -57.11) * mm});
            skLineSegment(sketch, "E327", {"start": v(-80, -57.11) * mm, "end": v(-80, -55.51) * mm});
            skLineSegment(sketch, "E328", {"start": v(-80, -68.11) * mm, "end": v(-97, -68.11) * mm});
            skLineSegment(sketch, "E329", {"start": v(-97, -68.11) * mm, "end": v(-97, -69.71) * mm});
            skLineSegment(sketch, "E330", {"start": v(-97, -69.71) * mm, "end": v(-80, -69.71) * mm});
            skLineSegment(sketch, "E331", {"start": v(-80, -69.71) * mm, "end": v(-80, -68.11) * mm});
            skLineSegment(sketch, "E332", {"start": v(-80, -80.71) * mm, "end": v(-97, -80.71) * mm});
            skLineSegment(sketch, "E333", {"start": v(-97, -80.71) * mm, "end": v(-97, -82.31) * mm});
            skLineSegment(sketch, "E334", {"start": v(-97, -82.31) * mm, "end": v(-80, -82.31) * mm});
            skLineSegment(sketch, "E335", {"start": v(-80, -82.31) * mm, "end": v(-80, -80.71) * mm});
            skLineSegment(sketch, "E336", {"start": v(-80, -93.31) * mm, "end": v(-97, -93.31) * mm});
            skLineSegment(sketch, "E337", {"start": v(-97, -93.31) * mm, "end": v(-97, -94.91) * mm});
            skPoint(sketch, "E337.endSnap0", {"position": v(-80.9, -94.91) * mm});
            skLineSegment(sketch, "E338", {"start": v(-97, -94.91) * mm, "end": v(-80, -94.91) * mm});
            skLineSegment(sketch, "E339", {"start": v(-80, -94.91) * mm, "end": v(-80, -93.31) * mm});
            skSolve(sketch);
        }
        {
            var Q0;
            Q0 = qSketchRegion(id + "F28", true);
            extrude(context, id + "F29", {"entities" : qUnion([Q0]), "operationType" : NewBodyOperationType.REMOVE, "oppositeDirection" : true, "depth" : 1.8 * mm});
        }
        {
            var Q0;
            Q0=makeQuery(id+"F1.opExtrude","SWEPT_FACE",FACE,{"disambiguationData":[OSD([sQuery(id+"F0.wireOp",EDGE,"E14.2.0.4")])]});
            var sketch = newSketch(context, id + "F30", { "sketchPlane" : qUnion([Q0])});
            skPoint(sketch, "E340.0", {"position": v(-80, -5.11) * mm});
            skPoint(sketch, "E341.0", {"position": v(-80, -6.7) * mm});
            skPoint(sketch, "E342.0", {"position": v(-80, -17.7) * mm});
            skPoint(sketch, "E343.0", {"position": v(-80, -19.3) * mm});
            skPoint(sketch, "E344.0", {"position": v(-80, -30.31) * mm});
            skPoint(sketch, "E345.0", {"position": v(-80, -31.9) * mm});
            skPoint(sketch, "E346.0", {"position": v(-80, -42.91) * mm});
            skPoint(sketch, "E347.0", {"position": v(-80, -44.5) * mm});
            skPoint(sketch, "E348.0", {"position": v(-80, -55.51) * mm});
            skPoint(sketch, "E349.0", {"position": v(-80, -57.11) * mm});
            skPoint(sketch, "E350.0", {"position": v(-80, -68.11) * mm});
            skPoint(sketch, "E351.0", {"position": v(-80, -69.71) * mm});
            skPoint(sketch, "E352.0", {"position": v(-80, -80.71) * mm});
            skPoint(sketch, "E353.0", {"position": v(-80, -82.31) * mm});
            skPoint(sketch, "E354.0", {"position": v(-80, -93.31) * mm});
            skPoint(sketch, "E355.0", {"position": v(-80, -94.91) * mm});
            skLineSegment(sketch, "E356", {"start": v(-17, -5.11) * mm, "end": v(0, -5.11) * mm});
            skLineSegment(sketch, "E357", {"start": v(0, -5.1) * mm, "end": v(0, -6.7) * mm});
            skLineSegment(sketch, "E358", {"start": v(0, -6.7) * mm, "end": v(-17, -6.7) * mm});
            skLineSegment(sketch, "E359", {"start": v(-17, -6.7) * mm, "end": v(-17, -5.11) * mm});
            skLineSegment(sketch, "E360.bottom", {"start": v(-17, -17.7) * mm, "end": v(0, -17.7) * mm});
            skLineSegment(sketch, "E360.top", {"start": v(-17, -19.3) * mm, "end": v(0, -19.3) * mm});
            skLineSegment(sketch, "E360.left", {"start": v(-17, -17.7) * mm, "end": v(-17, -19.3) * mm});
            skLineSegment(sketch, "E360.right", {"start": v(0, -17.7) * mm, "end": v(0, -19.3) * mm});
            skLineSegment(sketch, "E361.bottom", {"start": v(-17, -30.31) * mm, "end": v(0, -30.31) * mm});
            skLineSegment(sketch, "E361.top", {"start": v(-17, -31.9) * mm, "end": v(0, -31.9) * mm});
            skLineSegment(sketch, "E361.left", {"start": v(-17, -30.31) * mm, "end": v(-17, -31.9) * mm});
            skLineSegment(sketch, "E361.right", {"start": v(0, -30.31) * mm, "end": v(0, -31.9) * mm});
            skLineSegment(sketch, "E362.bottom", {"start": v(-17, -42.91) * mm, "end": v(0, -42.91) * mm});
            skLineSegment(sketch, "E362.top", {"start": v(-17, -44.5) * mm, "end": v(0, -44.5) * mm});
            skLineSegment(sketch, "E362.left", {"start": v(-17, -42.91) * mm, "end": v(-17, -44.5) * mm});
            skLineSegment(sketch, "E362.right", {"start": v(0, -42.91) * mm, "end": v(0, -44.5) * mm});
            skLineSegment(sketch, "E363.bottom", {"start": v(-17, -55.51) * mm, "end": v(0, -55.51) * mm});
            skLineSegment(sketch, "E363.top", {"start": v(-17, -57.11) * mm, "end": v(0, -57.11) * mm});
            skLineSegment(sketch, "E363.left", {"start": v(-17, -55.51) * mm, "end": v(-17, -57.11) * mm});
            skLineSegment(sketch, "E363.right", {"start": v(0, -55.51) * mm, "end": v(0, -57.11) * mm});
            skLineSegment(sketch, "E364.bottom", {"start": v(-17, -68.11) * mm, "end": v(0, -68.11) * mm});
            skLineSegment(sketch, "E364.top", {"start": v(-17, -69.71) * mm, "end": v(0, -69.71) * mm});
            skLineSegment(sketch, "E364.left", {"start": v(-17, -68.11) * mm, "end": v(-17, -69.71) * mm});
            skLineSegment(sketch, "E364.right", {"start": v(0, -68.11) * mm, "end": v(0, -69.71) * mm});
            skLineSegment(sketch, "E365.bottom", {"start": v(-17, -80.71) * mm, "end": v(0, -80.71) * mm});
            skLineSegment(sketch, "E365.top", {"start": v(-17, -82.31) * mm, "end": v(0, -82.31) * mm});
            skLineSegment(sketch, "E365.left", {"start": v(-17, -80.71) * mm, "end": v(-17, -82.31) * mm});
            skLineSegment(sketch, "E365.right", {"start": v(0, -80.71) * mm, "end": v(0, -82.31) * mm});
            skLineSegment(sketch, "E366.bottom", {"start": v(-17, -93.31) * mm, "end": v(0, -93.31) * mm});
            skLineSegment(sketch, "E366.top", {"start": v(-17, -94.91) * mm, "end": v(0, -94.91) * mm});
            skLineSegment(sketch, "E366.left", {"start": v(-17, -93.31) * mm, "end": v(-17, -94.91) * mm});
            skLineSegment(sketch, "E366.right", {"start": v(0, -93.31) * mm, "end": v(0, -94.91) * mm});
            skSolve(sketch);
        }
        {
            var Q0;
            Q0 = qSketchRegion(id + "F30", true);
            extrude(context, id + "F31", {"entities" : qUnion([Q0]), "operationType" : NewBodyOperationType.REMOVE, "oppositeDirection" : true, "depth" : 1.8 * mm});
        }
        {
            var Q0;
            Q0=makeQuery(id+"F1.opExtrude","SWEPT_FACE",FACE,{"disambiguationData":[OSD([sQuery(id+"F0.wireOp",EDGE,"E14.2.0.9"),sQuery(id+"F0.wireOp",EDGE,"E14.2.0.11")])]});
            var sketch = newSketch(context, id + "F32", { "sketchPlane" : qUnion([Q0])});
            skLineSegment(sketch, "E367.bottom", {"start": v(17, -6.7) * mm, "end": v(0, -6.7) * mm});
            skLineSegment(sketch, "E367.top", {"start": v(17, -5.11) * mm, "end": v(0, -5.11) * mm});
            skLineSegment(sketch, "E367.left", {"start": v(17, -6.7) * mm, "end": v(17, -5.11) * mm});
            skLineSegment(sketch, "E367.right", {"start": v(0, -6.7) * mm, "end": v(0, -5.11) * mm});
            skLineSegment(sketch, "E368.bottom", {"start": v(17, -19.3) * mm, "end": v(0, -19.3) * mm});
            skLineSegment(sketch, "E368.top", {"start": v(17, -17.7) * mm, "end": v(0, -17.7) * mm});
            skLineSegment(sketch, "E368.left", {"start": v(17, -19.3) * mm, "end": v(17, -17.7) * mm});
            skLineSegment(sketch, "E368.right", {"start": v(0, -19.3) * mm, "end": v(0, -17.7) * mm});
            skLineSegment(sketch, "E369.bottom", {"start": v(17, -31.9) * mm, "end": v(0, -31.9) * mm});
            skLineSegment(sketch, "E369.top", {"start": v(17, -30.31) * mm, "end": v(0, -30.31) * mm});
            skLineSegment(sketch, "E369.left", {"start": v(17, -31.9) * mm, "end": v(17, -30.31) * mm});
            skLineSegment(sketch, "E369.right", {"start": v(0, -31.9) * mm, "end": v(0, -30.31) * mm});
            skLineSegment(sketch, "E370.bottom", {"start": v(17, -44.5) * mm, "end": v(0, -44.5) * mm});
            skLineSegment(sketch, "E370.top", {"start": v(17, -42.91) * mm, "end": v(0, -42.91) * mm});
            skLineSegment(sketch, "E370.left", {"start": v(17, -44.5) * mm, "end": v(17, -42.91) * mm});
            skLineSegment(sketch, "E370.right", {"start": v(0, -44.5) * mm, "end": v(0, -42.91) * mm});
            skLineSegment(sketch, "E371.bottom", {"start": v(17, -57.11) * mm, "end": v(0, -57.11) * mm});
            skLineSegment(sketch, "E371.top", {"start": v(17, -55.51) * mm, "end": v(0, -55.51) * mm});
            skLineSegment(sketch, "E371.left", {"start": v(17, -57.11) * mm, "end": v(17, -55.51) * mm});
            skLineSegment(sketch, "E371.right", {"start": v(0, -57.11) * mm, "end": v(0, -55.51) * mm});
            skLineSegment(sketch, "E372.bottom", {"start": v(17, -69.71) * mm, "end": v(0, -69.71) * mm});
            skLineSegment(sketch, "E372.top", {"start": v(17, -68.11) * mm, "end": v(0, -68.11) * mm});
            skLineSegment(sketch, "E372.left", {"start": v(17, -69.71) * mm, "end": v(17, -68.11) * mm});
            skLineSegment(sketch, "E372.right", {"start": v(0, -69.71) * mm, "end": v(0, -68.11) * mm});
            skLineSegment(sketch, "E373.bottom", {"start": v(17, -82.31) * mm, "end": v(0, -82.31) * mm});
            skLineSegment(sketch, "E373.top", {"start": v(17, -80.71) * mm, "end": v(0, -80.71) * mm});
            skLineSegment(sketch, "E373.left", {"start": v(17, -82.31) * mm, "end": v(17, -80.71) * mm});
            skLineSegment(sketch, "E373.right", {"start": v(0, -82.31) * mm, "end": v(0, -80.71) * mm});
            skLineSegment(sketch, "E374.bottom", {"start": v(17, -94.91) * mm, "end": v(0, -94.91) * mm});
            skLineSegment(sketch, "E374.top", {"start": v(17, -93.31) * mm, "end": v(0, -93.31) * mm});
            skLineSegment(sketch, "E374.left", {"start": v(17, -94.91) * mm, "end": v(17, -93.31) * mm});
            skLineSegment(sketch, "E374.right", {"start": v(0, -94.91) * mm, "end": v(0, -93.31) * mm});
            skSolve(sketch);
        }
        {
            var Q0;
            Q0 = qSketchRegion(id + "F32", true);
            extrude(context, id + "F33", {"entities" : qUnion([Q0]), "operationType" : NewBodyOperationType.REMOVE, "oppositeDirection" : true, "depth" : 1.8 * mm});
        }
    });
